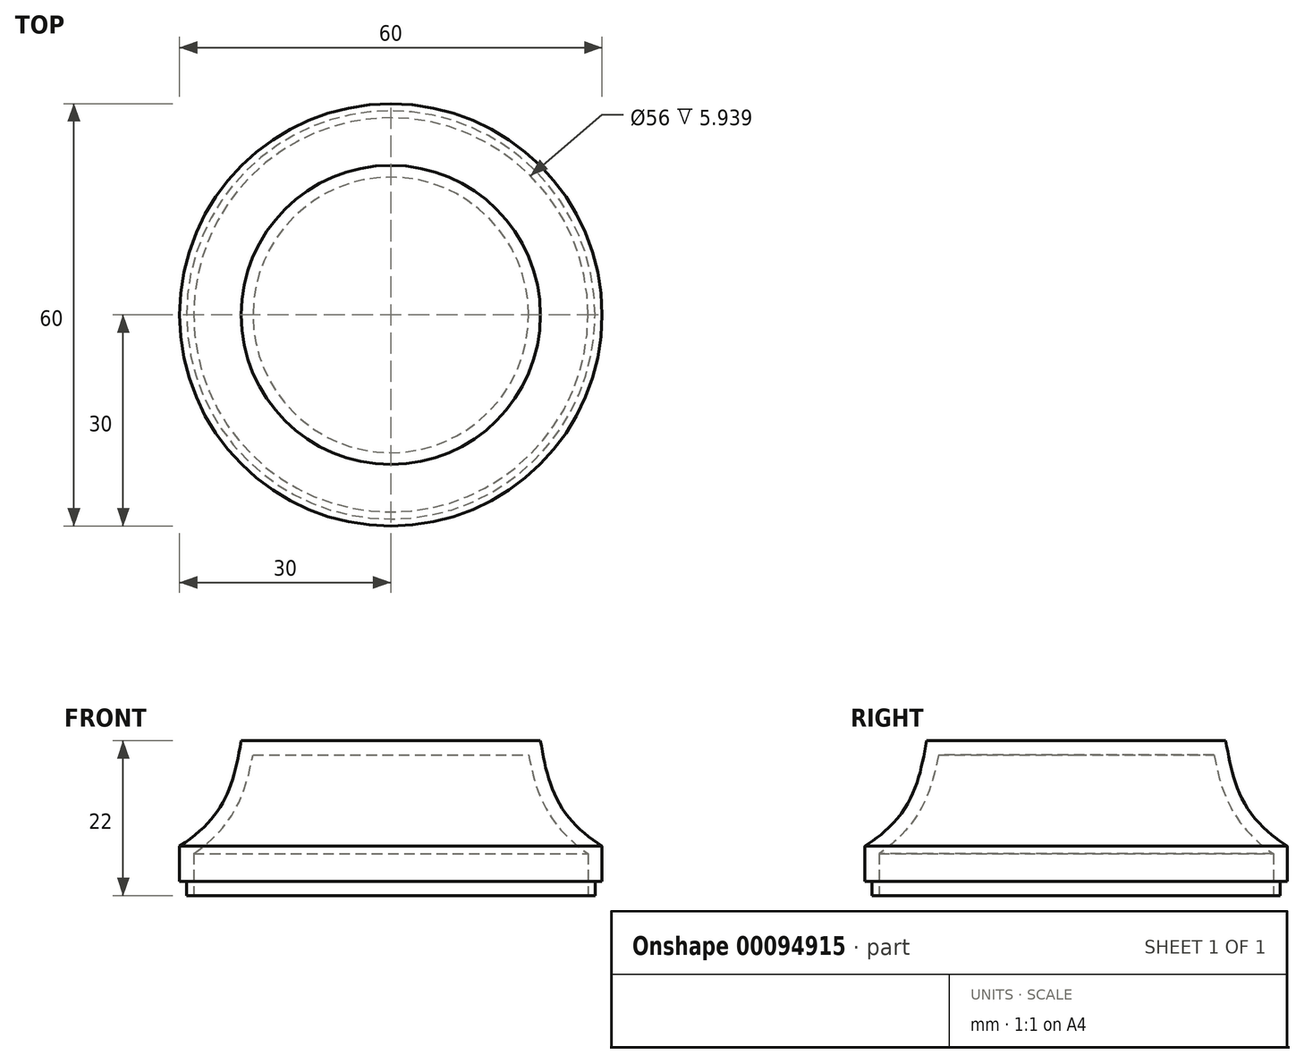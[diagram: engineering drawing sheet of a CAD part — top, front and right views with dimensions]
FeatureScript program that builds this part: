
annotation { "Feature Type Name" : "Feature", "Feature Type Description" : "" }
export const myFeature = defineFeature(function(context is Context, id is Id, definition is map)
    precondition{}
    {
        {
            var Q0;
            Q0=qCreatedBy(makeId("Front.planeOp"),FACE);
            var sketch = newSketch(context, id + "F0", { "sketchPlane" : qUnion([Q0])});
            skLineSegment(sketch, "E0", {"start": v(0, 0) * mm, "end": v(0, 20) * mm});
            skLineSegment(sketch, "E1", {"start": v(0, 20) * mm, "end": v(21.25, 20) * mm});
            skLineSegment(sketch, "E2", {"start": v(0, 0) * mm, "end": v(30, 0) * mm});
            skLineSegment(sketch, "E3", {"start": v(30, 0) * mm, "end": v(30, 5) * mm});
            skFitSpline(sketch, "E4", {"points": [v(30, 5) * mm, v(21.25, 20) * mm], "startDerivative": vector(-18.82, 12.26) * mm, "endDerivative": vector(-3.4, 20.27) * mm});
            skSolve(sketch);
        }
        {
            var Q0;
            Q0=makeQuery(id+"F0.imprint","IMPRINT",FACE,{"disambiguationData":[TD([[makeQuery(id+"F0.imprint","IMPRINT",EDGE,{"derivedFrom":sQuery(id+"F0.wireOp",EDGE,"E0")}),-1.0]])]});
            var Q1;
            Q1=sQuery(id+"F0.wireOp",EDGE,"E0");
            revolve(context, id + "F1", {"entities" : qUnion([Q0]), "axis" : qUnion([Q1]), "revolveType" : RevolveType.FULL});
        }
        {
            var Q0;
            Q0=makeQuery(id+"F1.opRevolve","SWEPT_FACE",FACE,{"disambiguationData":[OSD([sQuery(id+"F0.wireOp",EDGE,"E2")])]});
            shell(context, id + "F2", {"entities" : qUnion([Q0]), "thickness" : 2 * mm});
        }
        {
            var Q0;
            Q0=makeQuery(id+"F1.opRevolve","SWEPT_FACE",FACE,{"disambiguationData":[OSD([sQuery(id+"F0.wireOp",EDGE,"E2")])]});
            var sketch = newSketch(context, id + "F3", { "sketchPlane" : qUnion([Q0])});
            skCircle(sketch, "E5", {"center": v(0, 0) * mm, "radius": 28 * mm});
            skCircle(sketch, "E6", {"center": v(0, 0) * mm, "radius": 29 * mm});
            skSolve(sketch);
        }
        {
            var Q0;
            Q0=makeQuery(id+"F3.imprint","IMPRINT",FACE,{"disambiguationData":[TD([[makeQuery(id+"F3.imprint","IMPRINT",EDGE,{"derivedFrom":sQuery(id+"F3.wireOp",EDGE,"E5")}),-1.0]])]});
            extrude(context, id + "F4", {"entities" : qUnion([Q0]), "operationType" : NewBodyOperationType.ADD, "depth" : 2 * mm});
        }
    });
